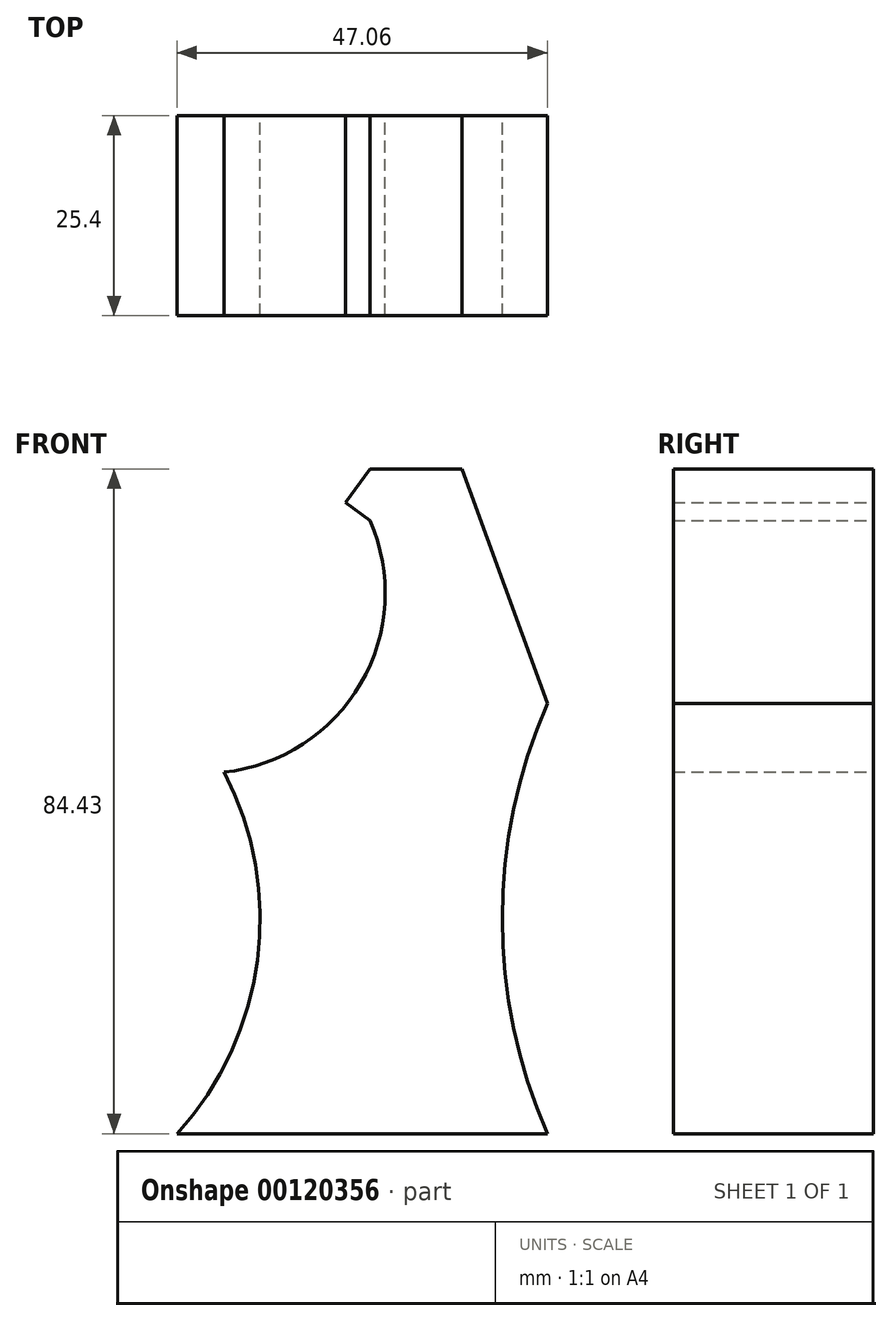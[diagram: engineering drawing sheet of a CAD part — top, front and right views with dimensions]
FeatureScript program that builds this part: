
annotation { "Feature Type Name" : "Feature", "Feature Type Description" : "" }
export const myFeature = defineFeature(function(context is Context, id is Id, definition is map)
    precondition{}
    {
        {
            var Q0;
            Q0=qCreatedBy(makeId("Front.planeOp"),FACE);
            var sketch = newSketch(context, id + "F0", { "sketchPlane" : qUnion([Q0])});
            skLineSegment(sketch, "E0", {"start": v(-24.53, -54.62) * mm, "end": v(22.53, -54.62) * mm});
            skArc(sketch, "E1", {"start": v(-24.53, -54.62) * mm, "mid": v(-14.3, -32.6) * mm, "end": v(-18.54, -8.7) * mm});
            skArc(sketch, "E2", {"start": v(-18.54, -8.7) * mm, "mid": v(-1.18, 2.58) * mm, "end": v(0, 23.25) * mm});
            skArc(sketch, "E3", {"start": v(22.53, 0) * mm, "mid": v(16.8, -27.31) * mm, "end": v(22.53, -54.62) * mm});
            skLineSegment(sketch, "E4", {"start": v(22.53, 0) * mm, "end": v(11.7, 29.8) * mm});
            skLineSegment(sketch, "E5", {"start": v(0, 29.8) * mm, "end": v(11.7, 29.8) * mm});
            skLineSegment(sketch, "E6", {"start": v(0, 29.8) * mm, "end": v(-3.14, 25.53) * mm});
            skLineSegment(sketch, "E7", {"start": v(-3.14, 25.53) * mm, "end": v(0, 23.25) * mm});
            skSolve(sketch);
        }
        {
            var Q0;
            Q0 = qSketchRegion(id + "F0", true);
            extrude(context, id + "F1", {"entities" : qUnion([Q0]), "endBound" : BoundingType.SYMMETRIC, "depth" : 25.4 * mm});
        }
    });
